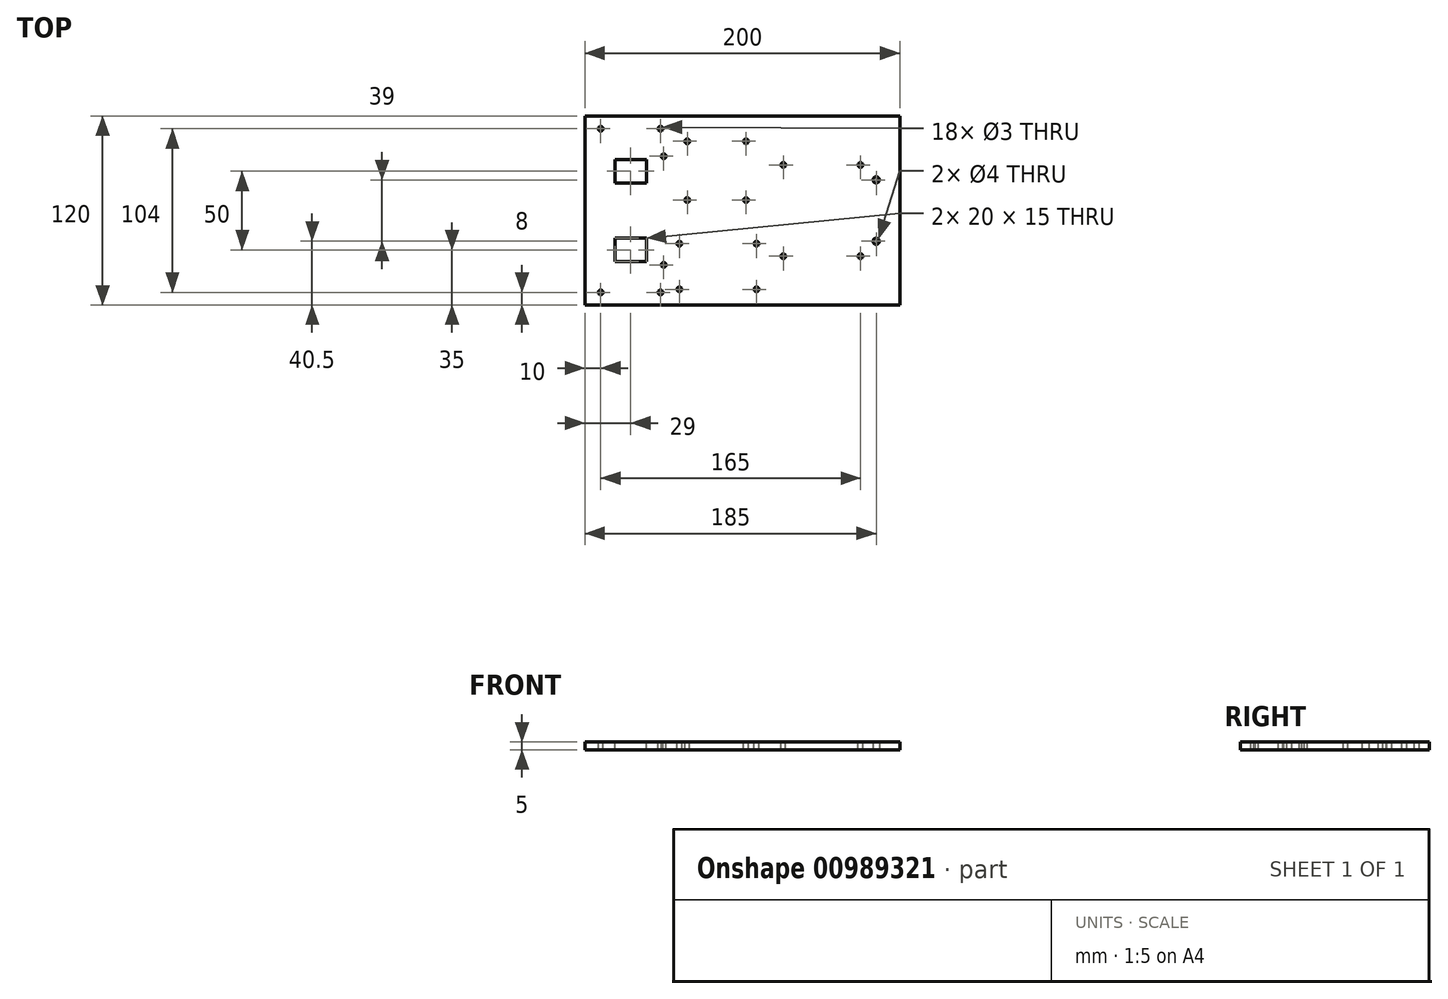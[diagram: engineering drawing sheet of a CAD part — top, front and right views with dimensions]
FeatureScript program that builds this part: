
annotation { "Feature Type Name" : "Feature", "Feature Type Description" : "" }
export const myFeature = defineFeature(function(context is Context, id is Id, definition is map)
    precondition{}
    {
        {
            var Q0;
            Q0=qCreatedBy(makeId("Top.planeOp"),FACE);
            var sketch = newSketch(context, id + "F0", { "sketchPlane" : qUnion([Q0])});
            skLineSegment(sketch, "E0.bottom", {"start": v(100, 60) * mm, "end": v(-100, 60) * mm});
            skLineSegment(sketch, "E0.top", {"start": v(100, -60) * mm, "end": v(-100, -60) * mm});
            skLineSegment(sketch, "E0.left", {"start": v(100, 60) * mm, "end": v(100, -60) * mm});
            skLineSegment(sketch, "E0.right", {"start": v(-100, 60) * mm, "end": v(-100, -60) * mm});
            skPoint(sketch, "E0.middle", {"position": v(0, 0) * mm});
            skSolve(sketch);
        }
        {
            var Q0;
            Q0=qSketchRegion(id+"F0",true);
            extrude(context, id + "F1", {"entities" : qUnion([Q0]), "depth" : 5 * mm, "offsetDistance" : 25 * mm});
        }
        {
            var Q0;
            Q0=makeQuery(id+"F1.opExtrude","CAP_FACE",FACE,{"disambiguationData":[OSD([sQuery(id+"F0.wireOp",EDGE,"E0.bottom"),sQuery(id+"F0.wireOp",EDGE,"E0.top"),sQuery(id+"F0.wireOp",EDGE,"E0.left"),sQuery(id+"F0.wireOp",EDGE,"E0.right"),sQuery(id+"F0.wireOp",EDGE,"IeUhD8lu-sktF-GMrU-8Srv-e3DhNs2p6vg7.bottom"),sQuery(id+"F0.wireOp",EDGE,"IeUhD8lu-sktF-GMrU-8Srv-e3DhNs2p6vg7.top"),sQuery(id+"F0.wireOp",EDGE,"IeUhD8lu-sktF-GMrU-8Srv-e3DhNs2p6vg7.left"),sQuery(id+"F0.wireOp",EDGE,"IeUhD8lu-sktF-GMrU-8Srv-e3DhNs2p6vg7.right")])],"isStart":false});
            var sketch = newSketch(context, id + "F2", { "sketchPlane" : qUnion([Q0])});
            skCircle(sketch, "E1", {"center": v(-90, 52) * mm, "radius": 1.5 * mm});
            skCircle(sketch, "E2", {"center": v(-52, 52) * mm, "radius": 1.5 * mm});
            skCircle(sketch, "E3.MirrorC", {"center": v(-90, -52) * mm, "radius": 1.5 * mm});
            skCircle(sketch, "E4.MirrorC", {"center": v(-52, -52) * mm, "radius": 1.5 * mm});
            skLineSegment(sketch, "E5", {"start": v(-90, -52) * mm, "end": v(-52, -52) * mm, "construction": true});
            skPoint(sketch, "E6", {"position": v(-71, -52) * mm});
            skLineSegment(sketch, "E7.bottom", {"start": v(-61, 17.5) * mm, "end": v(-81, 17.5) * mm});
            skLineSegment(sketch, "E7.top", {"start": v(-61, 32.5) * mm, "end": v(-81, 32.5) * mm});
            skLineSegment(sketch, "E7.left", {"start": v(-61, 17.5) * mm, "end": v(-61, 32.5) * mm});
            skLineSegment(sketch, "E7.right", {"start": v(-81, 17.5) * mm, "end": v(-81, 32.5) * mm});
            skPoint(sketch, "E7.middle", {"position": v(-71, 25) * mm});
            skLineSegment(sketch, "E8.MirrorCS", {"start": v(-61, -32.5) * mm, "end": v(-81, -32.5) * mm});
            skLineSegment(sketch, "E9.MirrorCS", {"start": v(-81, -17.5) * mm, "end": v(-81, -32.5) * mm});
            skLineSegment(sketch, "E10.MirrorCS", {"start": v(-61, -17.5) * mm, "end": v(-61, -32.5) * mm});
            skPoint(sketch, "E11.MirrorP", {"position": v(-71, -25) * mm});
            skLineSegment(sketch, "E12.MirrorCS", {"start": v(-61, -17.5) * mm, "end": v(-81, -17.5) * mm});
            skSolve(sketch);
        }
        {
            var Q0;
            Q0=qSketchRegion(id+"F2",true);
            extrude(context, id + "F3", {"entities" : qUnion([Q0]), "operationType" : NewBodyOperationType.REMOVE, "oppositeDirection" : true, "depth" : 25 * mm, "offsetDistance" : 25 * mm});
        }
        {
            var Q0;
            Q0=makeQuery(id+"F1.opExtrude","CAP_FACE",FACE,{"disambiguationData":[OSD([sQuery(id+"F0.wireOp",EDGE,"E0.bottom"),sQuery(id+"F0.wireOp",EDGE,"E0.top"),sQuery(id+"F0.wireOp",EDGE,"E0.left"),sQuery(id+"F0.wireOp",EDGE,"E0.right")])],"isStart":false});
            var sketch = newSketch(context, id + "F4", { "sketchPlane" : qUnion([Q0])});
            skCircle(sketch, "E13", {"center": v(26, -29) * mm, "radius": 1.5 * mm});
            skCircle(sketch, "E14.0.1.0", {"center": v(26, 29) * mm, "radius": 1.5 * mm});
            skCircle(sketch, "E14.1.0.0", {"center": v(75, -29) * mm, "radius": 1.5 * mm});
            skCircle(sketch, "E14.1.1.0", {"center": v(75, 29) * mm, "radius": 1.5 * mm});
            skLineSegment(sketch, "E14.direction1", {"start": v(26, -29) * mm, "end": v(75, -29) * mm, "construction": true});
            skLineSegment(sketch, "E14.direction2", {"start": v(26, -29) * mm, "end": v(26, 29) * mm, "construction": true});
            skPoint(sketch, "E15", {"position": v(26, 0) * mm});
            skSolve(sketch);
        }
        {
            var Q0;
            Q0=qSketchRegion(id+"F4",true);
            extrude(context, id + "F5", {"entities" : qUnion([Q0]), "operationType" : NewBodyOperationType.REMOVE, "endBound" : BoundingType.THROUGH_ALL, "oppositeDirection" : true, "depth" : 25 * mm, "offsetDistance" : 25 * mm});
        }
        {
            var Q0;
            Q0=makeQuery(id+"F1.opExtrude","CAP_FACE",FACE,{"disambiguationData":[OSD([sQuery(id+"F0.wireOp",EDGE,"E0.bottom"),sQuery(id+"F0.wireOp",EDGE,"E0.top"),sQuery(id+"F0.wireOp",EDGE,"E0.left"),sQuery(id+"F0.wireOp",EDGE,"E0.right")])],"isStart":true});
            var sketch = newSketch(context, id + "F6", { "sketchPlane" : qUnion([Q0])});
            skCircle(sketch, "E16", {"center": v(85, 19.5) * mm, "radius": 2 * mm});
            skCircle(sketch, "E17.MirrorC", {"center": v(85, -19.5) * mm, "radius": 2 * mm});
            skSolve(sketch);
        }
        {
            var Q0;
            Q0=qSketchRegion(id+"F6",true);
            extrude(context, id + "F7", {"entities" : qUnion([Q0]), "operationType" : NewBodyOperationType.REMOVE, "endBound" : BoundingType.THROUGH_ALL, "oppositeDirection" : true, "depth" : 25 * mm, "offsetDistance" : 25 * mm});
        }
        {
            var Q0;
            Q0=makeQuery(id+"F1.opExtrude","CAP_FACE",FACE,{"disambiguationData":[OSD([sQuery(id+"F0.wireOp",EDGE,"E0.bottom"),sQuery(id+"F0.wireOp",EDGE,"E0.top"),sQuery(id+"F0.wireOp",EDGE,"E0.left"),sQuery(id+"F0.wireOp",EDGE,"E0.right")])],"isStart":false});
            var sketch = newSketch(context, id + "F8", { "sketchPlane" : qUnion([Q0])});
            skCircle(sketch, "E18", {"center": v(-35, 44) * mm, "radius": 1.5 * mm});
            skCircle(sketch, "E19.0.1.0", {"center": v(-35, 6.7) * mm, "radius": 1.5 * mm});
            skCircle(sketch, "E19.1.0.0", {"center": v(2.3, 44) * mm, "radius": 1.5 * mm});
            skCircle(sketch, "E19.1.1.0", {"center": v(2.3, 6.7) * mm, "radius": 1.5 * mm});
            skLineSegment(sketch, "E19.direction1", {"start": v(-35, 44) * mm, "end": v(2.3, 44) * mm, "construction": true});
            skLineSegment(sketch, "E19.direction2", {"start": v(-35, 44) * mm, "end": v(-35, 6.7) * mm, "construction": true});
            skSolve(sketch);
        }
        {
            var Q0;
            Q0=qSketchRegion(id+"F8",true);
            extrude(context, id + "F9", {"entities" : qUnion([Q0]), "operationType" : NewBodyOperationType.REMOVE, "endBound" : BoundingType.THROUGH_ALL, "oppositeDirection" : true, "depth" : 25 * mm, "offsetDistance" : 25 * mm});
        }
        {
            var Q0;
            Q0=makeQuery(id+"F1.opExtrude","CAP_FACE",FACE,{"disambiguationData":[OSD([sQuery(id+"F0.wireOp",EDGE,"E0.bottom"),sQuery(id+"F0.wireOp",EDGE,"E0.top"),sQuery(id+"F0.wireOp",EDGE,"E0.left"),sQuery(id+"F0.wireOp",EDGE,"E0.right")])],"isStart":false});
            var sketch = newSketch(context, id + "F10", { "sketchPlane" : qUnion([Q0])});
            skCircle(sketch, "E20", {"center": v(-40, -21) * mm, "radius": 1.5 * mm});
            skCircle(sketch, "E21.0.1.0", {"center": v(-40, -50) * mm, "radius": 1.5 * mm});
            skCircle(sketch, "E21.1.0.0", {"center": v(9, -21) * mm, "radius": 1.5 * mm});
            skCircle(sketch, "E21.1.1.0", {"center": v(9, -50) * mm, "radius": 1.5 * mm});
            skLineSegment(sketch, "E21.direction1", {"start": v(-40, -21) * mm, "end": v(9, -21) * mm, "construction": true});
            skLineSegment(sketch, "E21.direction2", {"start": v(-40, -21) * mm, "end": v(-40, -50) * mm, "construction": true});
            skSolve(sketch);
        }
        {
            var Q0;
            Q0=qSketchRegion(id+"F10",true);
            extrude(context, id + "F11", {"entities" : qUnion([Q0]), "operationType" : NewBodyOperationType.REMOVE, "endBound" : BoundingType.THROUGH_ALL, "oppositeDirection" : true, "depth" : 25 * mm, "offsetDistance" : 25 * mm});
        }
        {
            var Q0;
            Q0=makeQuery(id+"F1.opExtrude","CAP_FACE",FACE,{"disambiguationData":[OSD([sQuery(id+"F0.wireOp",EDGE,"E0.bottom"),sQuery(id+"F0.wireOp",EDGE,"E0.top"),sQuery(id+"F0.wireOp",EDGE,"E0.left"),sQuery(id+"F0.wireOp",EDGE,"E0.right")])],"isStart":false});
            var sketch = newSketch(context, id + "F12", { "sketchPlane" : qUnion([Q0])});
            skCircle(sketch, "E22", {"center": v(-50, 34.5) * mm, "radius": 1.5 * mm});
            skCircle(sketch, "E23", {"center": v(-50, -34.5) * mm, "radius": 1.5 * mm});
            skLineSegment(sketch, "E24", {"start": v(-50, 34.5) * mm, "end": v(-50, -34.5) * mm, "construction": true});
            skPoint(sketch, "E25", {"position": v(-50, 0) * mm});
            skSolve(sketch);
        }
        {
            var Q0;
            Q0=qSketchRegion(id+"F12",true);
            extrude(context, id + "F13", {"entities" : qUnion([Q0]), "operationType" : NewBodyOperationType.REMOVE, "endBound" : BoundingType.THROUGH_ALL, "oppositeDirection" : true, "depth" : 25 * mm, "offsetDistance" : 25 * mm});
        }
    });
